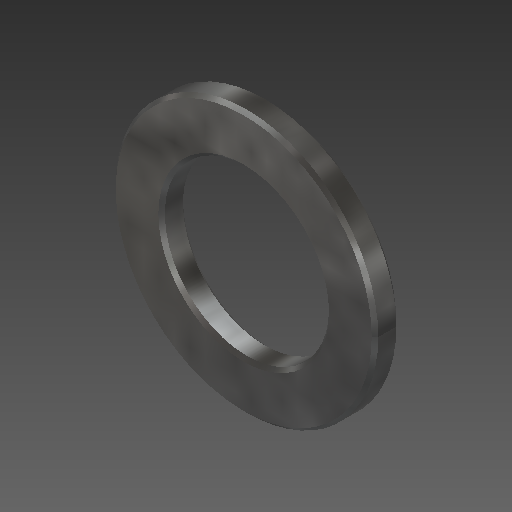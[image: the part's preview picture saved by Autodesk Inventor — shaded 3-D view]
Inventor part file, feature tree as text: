
AUTODESK INVENTOR PART (.ipt)
format: ipt  version: 2018 (Build 220112000, 112)  size: 137,216 bytes
history: native  units: mm
features: extrude x1, chamfer x1, sketch x1
ambient origin geometry x8: Origin, YZ Plane, XZ Plane, XY Plane, X Axis, Y Axis, Z Axis, Center Point
bodies: Solid1 (feature_tree)
feature tree (3):
  extrude  "Extrusion1"  Depth=1.5mm
  chamfer  "Chamfer1"  Distance=1.5mm
  sketch  "Sketch1"  dims[d0=10.0mm d1=16.0mm d2=1.5mm d3=0.0mm d4=0.2mm d5=2.0mm d6=45.0deg]
